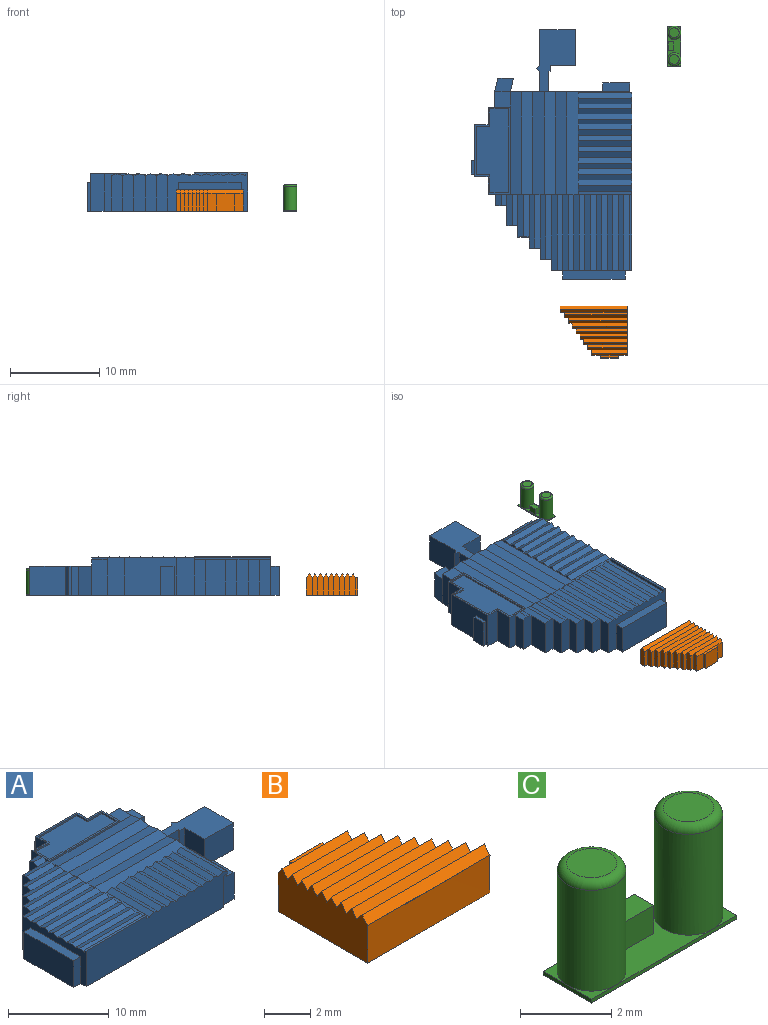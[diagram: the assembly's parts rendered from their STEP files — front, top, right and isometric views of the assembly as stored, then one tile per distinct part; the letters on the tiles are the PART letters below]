
ASSEMBLY  parts=3 mates=2
PART A: 138 faces, bbox 28x18x4.3 mm
  f0: plane 3.25x0.4mm, normal (1,0,0), area 1.3mm2, adj f44,f46,f65,f137
  f1: plane 4x3.25mm, normal (0,-1,0), area 13mm2, adj f2,f6,f65,f136
  f2: plane 4x3.25mm, normal (1,0,0), area 13mm2, adj f1,f7,f65,f136
  f3: plane 3.25x2.29mm, normal (0,-1,0), area 7.5mm2, adj f4,f39,f65,f136
  f4: plane 3.25x0.2mm, normal (-1,0,0), area 0.7mm2, adj f3,f5,f65,f136
  f5: plane 3.25x0.67mm, normal (0,-1,0), area 2.2mm2, adj f4,f6,f65,f136
  f6: plane 3.25x2.8mm, normal (-1,0,0), area 9.1mm2, adj f1,f5,f65,f136
  f7: plane 4x3.25mm, normal (0,1,0), area 13mm2, adj f2,f8,f65,f136
  f8: plane 3.25x0.38mm, normal (0.75,0.66,0), area 1.6mm2, adj f7,f9,f65,f136
  f9: plane 3.25x0.38mm, normal (-0.75,0.66,0), area 1.6mm2, adj f8,f10,f65,f136
  f10: plane 3.25x2.29mm, normal (0,1,0), area 7.5mm2, adj f9,f39,f65,f136
  f11: plane 3.25x1.5mm, normal (-0.22,-0.97,0), area 5mm2, adj f12,f39,f65,f135
  f12: plane 3.25x1.75mm, normal (1,0,0), area 5.7mm2, adj f11,f13,f65,f135
  f13: plane 3.25x1.5mm, normal (0.22,0.97,0), area 5mm2, adj f12,f40,f65,f135
  f14: plane 7.25x0.63mm, normal (0,-0.3,0.95), area 4.8mm2, adj f15,f29,f59,f109,f134
  f15: plane 7.25x0.63mm, normal (0,0.3,0.95), area 4.8mm2, adj f14,f16,f28,f58,f59,f109
  f16: plane 6x0.63mm, normal (0,-0.3,0.95), area 3.9mm2, adj f15,f17,f28,f57,f111
  f17: plane 6x0.63mm, normal (0,0.3,0.95), area 3.9mm2, adj f16,f18,f31,f56,f57,f111
  f18: plane 4.75x0.63mm, normal (0,-0.3,0.95), area 3.1mm2, adj f17,f19,f31,f55,f112
  f19: plane 4.75x0.63mm, normal (0,0.3,0.95), area 3.1mm2, adj f18,f20,f30,f54,f55,f112
  f20: plane 3.5x0.63mm, normal (0,-0.3,0.95), area 2.3mm2, adj f19,f21,f30,f53,f113
  f21: plane 3.5x0.63mm, normal (0,0.3,0.95), area 2.3mm2, adj f20,f22,f49,f52,f53,f113
  f22: plane 1.25x0.63mm, normal (0,-0.3,0.95), area 0.8mm2, adj f21,f23,f49,f51
  f23: plane 1.25x0.63mm, normal (0,0.3,0.95), area 0.8mm2, adj f22,f25,f50,f51
  f24: plane 6x0.39mm, normal (0,0,1), area 2.3mm2, adj f64,f68,f100,f107,f114,f115,f116,f117
  f25: plane 4.2x1.48mm, normal (-1,0,0), area 3.6mm2, adj f23,f48,f50,f65,f98
  f26: plane 0.84x0.2mm, normal (-1,0,0), area 0.1mm2, adj f100,f105,f132,f133
  f27: plane 0.65x0.16mm, normal (-1,0,0), area 0mm2, adj f100,f130,f131
  f28: plane 0.84x0.2mm, normal (-1,0,0), area 0.1mm2, adj f15,f16,f103,f104
  f29: plane 0.61x0.15mm, normal (-1,0,0), area 0mm2, adj f14,f104,f134
  f30: plane 0.84x0.2mm, normal (-1,0,0), area 0.1mm2, adj f19,f20,f101,f102
  f31: plane 0.56x0.13mm, normal (-1,0,0), area 0mm2, adj f17,f18,f102
  f32: plane 5.75x0.1mm, normal (0,0,1), area 0.6mm2, adj f37,f39,f67,f100
  f33: plane 3.25x3mm, normal (1,0,0), area 9.8mm2, adj f34,f37,f65,f106
  f34: plane 3.25x1mm, normal (0,1,0), area 3.2mm2, adj f33,f39,f65,f106
  f35: plane 1.75x1.7mm, normal (0,0,1), area 3mm2, adj f39,f40,f41,f101
  f36: plane 7x3.25mm, normal (-1,0,0), area 22.8mm2, adj f61,f62,f65,f88
  f37: plane 4x1.75mm, normal (0,-1,0), area 6.1mm2, adj f32,f33,f38,f39,f65,f66,f67,f106
  f38: plane 3.79x0.25mm, normal (1,0,0), area 0.9mm2, adj f37,f64,f65,f66
  f39: plane 15.1x4.2mm, normal (1,0,0), area 42.5mm2, adj f3,f10,f11,f32,f34,f35,f37,f40
  f40: plane 4x1.7mm, normal (0,1,0), area 6.8mm2, adj f13,f35,f39,f41,f65
  f41: plane 4.2x2.5mm, normal (1,0,0), area 3.5mm2, adj f35,f40,f42,f65,f96,f98
  f42: plane 4.2x2mm, normal (0,1,0), area 8.4mm2, adj f41,f43,f65,f98
  f43: plane 4.2x1.5mm, normal (1,0,0), area 6.3mm2, adj f42,f46,f65,f98
  f44: plane 3.25x1.5mm, normal (0,1,0), area 4.9mm2, adj f0,f45,f65,f137
  f45: plane 3.25x0.4mm, normal (-1,0,0), area 1.3mm2, adj f44,f46,f65,f137
  f46: plane 5.8x4.2mm, normal (0,1,0), area 19.5mm2, adj f0,f43,f45,f47,f65,f98,f137
  f47: plane 4.2x1.5mm, normal (-1,0,0), area 6.3mm2, adj f46,f48,f65,f98
  f48: plane 4.2x2mm, normal (0,1,0), area 8.4mm2, adj f25,f47,f65,f98
  f49: plane 1.03x0.2mm, normal (-1,0,0), area 0.1mm2, adj f21,f22,f96,f98
  f50: plane 4x1.25mm, normal (0,1,0), area 5mm2, adj f23,f25,f51,f65
  f51: plane 4.2x1.25mm, normal (-1,0,0), area 5.1mm2, adj f22,f23,f50,f52,f65
  f52: plane 4x2.25mm, normal (0,1,0), area 9mm2, adj f21,f51,f53,f65
  f53: plane 4.2x1.25mm, normal (-1,0,0), area 5.1mm2, adj f20,f21,f52,f54,f65
  f54: plane 4x1.25mm, normal (0,1,0), area 5mm2, adj f19,f53,f55,f65
  f55: plane 4.2x1.25mm, normal (-1,0,0), area 5.1mm2, adj f18,f19,f54,f56,f65
  f56: plane 4x1.25mm, normal (0,1,0), area 5mm2, adj f17,f55,f57,f65
  f57: plane 4.2x1.25mm, normal (-1,0,0), area 5.1mm2, adj f16,f17,f56,f58,f65
  f58: plane 4x1.25mm, normal (0,1,0), area 5mm2, adj f15,f57,f59,f65
  f59: plane 4.2x1.25mm, normal (-1,0,0), area 5.1mm2, adj f14,f15,f58,f60,f65
  f60: plane 4x1.25mm, normal (0,1,0), area 5mm2, adj f59,f63,f65,f134
  f61: plane 3.25x1mm, normal (0,1,0), area 3.3mm2, adj f36,f63,f65,f88
  f62: plane 3.25x1mm, normal (0,-1,0), area 3.3mm2, adj f36,f63,f65,f88
  f63: plane 9x4.32mm, normal (-1,0,0), area 14.2mm2, adj f60,f61,f62,f64,f65,f88,f119,f120
  f64: plane 19.9x4.32mm, normal (0,-1,0), area 81.6mm2, adj f24,f38,f63,f65,f66,f67,f68,f69
  f65: plane 27.96x18mm, normal (0,0,-1), area 329.8mm2, adj f0,f1,f2,f3,f4,f5,f6,f7
  f66: plane 0.65x0.25mm, normal (0,0,-1), area 0.2mm2, adj f37,f38,f64,f67
  f67: plane 6x0.22mm, normal (1,0,0), area 0.1mm2, adj f32,f37,f64,f66,f69,f87
  f68: plane 6x0.02mm, normal (-1,0,0), area 0.1mm2, adj f24,f64,f86,f87
  f69: plane 6x0.63mm, normal (0.44,0,0.9), area 4.2mm2, adj f64,f67,f70,f87
  f70: plane 6x0.63mm, normal (-0.43,0,0.9), area 4.2mm2, adj f64,f69,f71,f87
  f71: plane 6x0.56mm, normal (0.47,0,0.88), area 3.8mm2, adj f64,f70,f72,f87
  f72: plane 6x0.56mm, normal (-0.47,0,0.88), area 3.8mm2, adj f64,f71,f73,f87
  f73: plane 6x0.56mm, normal (0.47,0,0.88), area 3.8mm2, adj f64,f72,f74,f87
  f74: plane 6x0.56mm, normal (-0.47,0,0.88), area 3.8mm2, adj f64,f73,f75,f87
  f75: plane 6x0.63mm, normal (0.43,0,0.9), area 4.2mm2, adj f64,f74,f76,f87
  f76: plane 6x0.63mm, normal (-0.43,0,0.9), area 4.2mm2, adj f64,f75,f77,f87
  f77: plane 6x0.63mm, normal (0.43,0,0.9), area 4.2mm2, adj f64,f76,f78,f87
  f78: plane 6x0.63mm, normal (-0.43,0,0.9), area 4.2mm2, adj f64,f77,f79,f87
  f79: plane 6x0.63mm, normal (0.43,0,0.9), area 4.2mm2, adj f64,f78,f80,f87
  f80: plane 6x0.63mm, normal (-0.43,0,0.9), area 4.2mm2, adj f64,f79,f81,f87
  f81: plane 6x0.63mm, normal (0.43,0,0.9), area 4.2mm2, adj f64,f80,f82,f87
  f82: plane 6x0.63mm, normal (-0.43,0,0.9), area 4.2mm2, adj f64,f81,f83,f87
  f83: plane 6x0.63mm, normal (0.43,0,0.9), area 4.2mm2, adj f64,f82,f84,f87
  f84: plane 6x0.63mm, normal (-0.43,0,0.9), area 4.2mm2, adj f64,f83,f85,f87
  f85: plane 6x0.63mm, normal (0.43,0,0.9), area 4.2mm2, adj f64,f84,f86,f87
  f86: plane 6x0.63mm, normal (-0.43,0,0.9), area 4.2mm2, adj f64,f68,f85,f87
  f87: plane 11.01x0.32mm, normal (0,1,0), area 1.8mm2, adj f67,f68,f69,f70,f71,f72,f73,f74
  f88: plane 7x1mm, normal (0,0,1), area 7mm2, adj f36,f61,f62,f63
  f89: plane 9.4x0.2mm, normal (0,1,0), area 1.9mm2, adj f90,f97,f98,f99
  f90: plane 2.1x0.2mm, normal (1,0,0), area 0.4mm2, adj f89,f91,f98,f99
  f91: plane 2x0.2mm, normal (0,-1,0), area 0.4mm2, adj f90,f92,f98,f99
  f92: plane 1.5x0.2mm, normal (1,0,0), area 0.3mm2, adj f91,f93,f98,f99
  f93: plane 5.4x0.2mm, normal (0,-1,0), area 1.1mm2, adj f92,f94,f98,f99
  f94: plane 1.5x0.2mm, normal (-1,0,0), area 0.3mm2, adj f93,f95,f98,f99
  f95: plane 2x0.2mm, normal (0,-1,0), area 0.4mm2, adj f94,f97,f98,f99
  f96: plane 9.8x0.2mm, normal (0,-1,0), area 2mm2, adj f41,f49,f98,f101,f113
  f97: plane 2.1x0.2mm, normal (-1,0,0), area 0.4mm2, adj f89,f95,f98,f99
  f98: plane 9.8x4mm, normal (0,0,1), area 5.4mm2, adj f25,f41,f42,f43,f46,f47,f48,f49
  f99: plane 9.4x3.6mm, normal (0,0,1), area 27.8mm2, adj f89,f90,f91,f92,f93,f94,f95,f97
  f100: plane 11.5x1.27mm, normal (0,-0.16,0.99), area 14.8mm2, adj f24,f26,f27,f32,f39,f87,f105,f107
  f101: plane 11.5x1.27mm, normal (0,0.16,0.99), area 14.7mm2, adj f30,f35,f39,f96,f102,f113
  f102: plane 11.5x1.27mm, normal (0,-0.16,0.99), area 14.8mm2, adj f30,f31,f39,f101,f103,f111,f112
  f103: plane 11.5x1.26mm, normal (0,0.16,0.99), area 14.7mm2, adj f28,f39,f102,f104,f111
  f104: plane 11.5x1.27mm, normal (0,-0.16,0.99), area 14.8mm2, adj f28,f29,f39,f103,f105,f109,f110
  f105: plane 11.5x1.26mm, normal (0,0.16,0.99), area 14.7mm2, adj f26,f39,f100,f104,f110
  f106: plane 3x1mm, normal (0,0,1), area 3mm2, adj f33,f34,f37,f39
  f107: plane 1.09x0.2mm, normal (1,0,0), area 0.1mm2, adj f24,f100,f129,f130
  f108: plane 0.19x0.04mm, normal (1,0,0), area 0mm2, adj f100,f131,f132
  f109: plane 0.23x0.06mm, normal (1,0,0), area 0mm2, adj f14,f15,f104
  f110: plane 0.84x0.2mm, normal (1,0,0), area 0.1mm2, adj f104,f105,f133,f134
  f111: plane 0.84x0.2mm, normal (1,0,0), area 0.1mm2, adj f16,f17,f102,f103
  f112: plane 0.27x0.07mm, normal (1,0,0), area 0mm2, adj f18,f19,f102
  f113: plane 0.57x0.2mm, normal (1,0,0), area 0.1mm2, adj f20,f21,f96,f101
  f114: plane 1.25x0.2mm, normal (1,0,0), area 0.1mm2, adj f24,f127,f128
  f115: plane 1.25x0.2mm, normal (1,0,0), area 0.1mm2, adj f24,f125,f126
  f116: plane 1.25x0.2mm, normal (1,0,0), area 0.1mm2, adj f24,f123,f124
  f117: plane 1.25x0.2mm, normal (1,0,0), area 0.1mm2, adj f24,f121,f122
  f118: plane 0.32x0.25mm, normal (1,0,0), area 0.1mm2, adj f24,f64,f119,f120
  f119: plane 8.5x0.25mm, normal (0,0,1), area 2.1mm2, adj f63,f64,f118,f120
  f120: plane 8.5x0.32mm, normal (0,1,0.01), area 2.7mm2, adj f63,f118,f119,f121
  f121: plane 8.5x0.63mm, normal (0,-0.3,0.95), area 5.6mm2, adj f63,f117,f120,f122
  f122: plane 8.5x0.63mm, normal (0,0.3,0.95), area 5.6mm2, adj f63,f117,f121,f123
  f123: plane 8.5x0.63mm, normal (0,-0.3,0.95), area 5.6mm2, adj f63,f116,f122,f124
  f124: plane 8.5x0.63mm, normal (0,0.3,0.95), area 5.6mm2, adj f63,f116,f123,f125
  f125: plane 8.5x0.63mm, normal (0,-0.3,0.95), area 5.6mm2, adj f63,f115,f124,f126
  f126: plane 8.5x0.63mm, normal (0,0.3,0.95), area 5.6mm2, adj f63,f115,f125,f127
  f127: plane 8.5x0.63mm, normal (0,-0.3,0.95), area 5.6mm2, adj f63,f114,f126,f128
  f128: plane 8.5x0.63mm, normal (0,0.3,0.95), area 5.6mm2, adj f63,f114,f127,f129
  f129: plane 8.5x0.63mm, normal (0,-0.3,0.95), area 5.6mm2, adj f63,f107,f128,f130
  f130: plane 8.5x0.63mm, normal (0,0.3,0.95), area 5.6mm2, adj f27,f63,f107,f129,f131
  f131: plane 8.5x0.63mm, normal (0,-0.3,0.95), area 5.6mm2, adj f27,f63,f108,f130,f132
  f132: plane 8.5x0.63mm, normal (0,0.3,0.95), area 5.6mm2, adj f26,f63,f108,f131,f133
  f133: plane 8.5x0.63mm, normal (0,-0.3,0.95), area 5.6mm2, adj f26,f63,f110,f132,f134
  f134: plane 8.5x0.63mm, normal (0,0.3,0.95), area 5.6mm2, adj f14,f29,f60,f63,f110,f133
  f135: plane 2.1x1.5mm, normal (0,0,1), area 2.6mm2, adj f11,f12,f13,f39
  f136: plane 6.96x4.38mm, normal (0,0,1), area 19.2mm2, adj f1,f2,f3,f4,f5,f6,f7,f8
  f137: plane 1.5x0.4mm, normal (0,0,1), area 0.6mm2, adj f0,f44,f45,f46
PART B: 45 faces, bbox 7.5x5.8x2.4 mm
  f0: plane 2.42x0.71mm, normal (1,0,0), area 1.6mm2, adj f16,f24,f25,f41,f43,f44
  f1: plane 4x0.41mm, normal (0,-0.75,0.66), area 2.1mm2, adj f2,f4,f17,f23
  f2: plane 4.02x0.43mm, normal (0,0.85,0.52), area 1.9mm2, adj f1,f17,f18,f22,f23,f40
  f3: plane 4.43x0.41mm, normal (0,-0.77,0.64), area 2.3mm2, adj f4,f5,f23,f38
  f4: plane 4.43x0.41mm, normal (0,0.83,0.55), area 2.1mm2, adj f1,f3,f23,f38,f39
  f5: plane 4.86x0.41mm, normal (0,0.83,0.55), area 2.3mm2, adj f3,f6,f23,f36,f37,f38
  f6: plane 4.86x0.41mm, normal (0,-0.77,0.64), area 2.5mm2, adj f5,f7,f23,f36
  f7: plane 5.29x0.41mm, normal (0,0.83,0.55), area 2.5mm2, adj f6,f8,f23,f34,f35,f36
  f8: plane 5.29x0.41mm, normal (0,-0.77,0.64), area 2.8mm2, adj f7,f9,f23,f34
  f9: plane 5.72x0.41mm, normal (0,0.83,0.55), area 2.7mm2, adj f8,f10,f23,f32,f33,f34
  f10: plane 5.72x0.41mm, normal (0,-0.77,0.64), area 3mm2, adj f9,f11,f23,f32
  f11: plane 6.15x0.41mm, normal (0,0.83,0.55), area 3mm2, adj f10,f12,f23,f30,f31,f32
  f12: plane 6.15x0.41mm, normal (0,-0.77,0.64), area 3.2mm2, adj f11,f13,f23,f30
  f13: plane 6.58x0.41mm, normal (0,0.84,0.55), area 3.1mm2, adj f12,f14,f23,f28,f29,f30
  f14: plane 6.58x0.41mm, normal (0,-0.76,0.65), area 3.5mm2, adj f13,f15,f23,f28
  f15: plane 7.01x0.42mm, normal (0,0.78,0.62), area 3.6mm2, adj f14,f16,f23,f26,f27,f28
  f16: plane 7.5x0.42mm, normal (0,-0.82,0.57), area 3.4mm2, adj f0,f15,f23,f25,f26,f43
  f17: plane 2.41x0.6mm, normal (1,0,0), area 1.3mm2, adj f1,f2,f18,f39,f41
  f18: plane 2.02x1.02mm, normal (0,1,0), area 2mm2, adj f2,f17,f19,f41
  f19: plane 2x0.3mm, normal (1,0,0), area 0.6mm2, adj f18,f20,f40,f41
  f20: plane 2x2mm, normal (0,1,0), area 4mm2, adj f19,f21,f40,f41
  f21: plane 2x0.3mm, normal (-1,0,0), area 0.6mm2, adj f20,f22,f40,f41
  f22: plane 2x1mm, normal (0,1,0), area 2mm2, adj f2,f21,f23,f41
  f23: plane 5.5x2.4mm, normal (-1,0,0), area 12.1mm2, adj f1,f2,f3,f4,f5,f6,f7,f8
  f24: plane 7.5x2mm, normal (0,-1,0), area 15mm2, adj f0,f23,f41,f42
  f25: plane 2.02x0.49mm, normal (0,1,0), area 1mm2, adj f0,f16,f26,f41
  f26: plane 2.42x0.6mm, normal (1,0,0), area 1.3mm2, adj f15,f16,f25,f27,f41
  f27: plane 2.01x0.43mm, normal (0,1,0), area 0.9mm2, adj f15,f26,f28,f41
  f28: plane 2.41x0.6mm, normal (1,0,0), area 1.3mm2, adj f13,f14,f15,f27,f29,f41
  f29: plane 2.02x0.43mm, normal (0,1,0), area 0.9mm2, adj f13,f28,f30,f41
  f30: plane 2.41x0.6mm, normal (1,0,0), area 1.3mm2, adj f11,f12,f13,f29,f31,f41
  f31: plane 2.01x0.43mm, normal (0,1,0), area 0.9mm2, adj f11,f30,f32,f41
  f32: plane 2.41x0.6mm, normal (1,0,0), area 1.3mm2, adj f9,f10,f11,f31,f33,f41
  f33: plane 2.01x0.43mm, normal (0,1,0), area 0.9mm2, adj f9,f32,f34,f41
  f34: plane 2.41x0.6mm, normal (1,0,0), area 1.3mm2, adj f7,f8,f9,f33,f35,f41
  f35: plane 2.01x0.43mm, normal (0,1,0), area 0.9mm2, adj f7,f34,f36,f41
  f36: plane 2.41x0.6mm, normal (1,0,0), area 1.3mm2, adj f5,f6,f7,f35,f37,f41
  f37: plane 2.01x0.43mm, normal (0,1,0), area 0.9mm2, adj f5,f36,f38,f41
  f38: plane 2.41x0.6mm, normal (1,0,0), area 1.3mm2, adj f3,f4,f5,f37,f39,f41
  f39: plane 2.01x0.43mm, normal (0,1,0), area 0.9mm2, adj f4,f17,f38,f41
  f40: plane 2.01x0.31mm, normal (0,0,1), area 0.6mm2, adj f2,f19,f20,f21
  f41: plane 7.5x5.8mm, normal (0,0,-1), area 32.3mm2, adj f0,f17,f18,f19,f20,f21,f22,f23
  f42: plane 7.5x0.02mm, normal (0,0,-1), area 0.1mm2, adj f24,f44
  f43: plane 7.5x0.42mm, normal (0,0.74,0.67), area 4mm2, adj f0,f16,f23,f44
  f44: plane 7.5x0.42mm, normal (0,-0.76,0.65), area 4.1mm2, adj f0,f23,f42,f43
PART C: 21 faces, bbox 4.6x1.6x3 mm
  f0: cylinder r=0.75mm len=2.7mm, axis (0,0,-1), area 12.7mm2, adj f2,f5,f6,f13
  f1: plane 1.1x1.1mm, normal (0,0,1), area 1mm2, adj f2
  f2: torus R=0.55mm, axis (0,0,1), area 1.3mm2, adj f0,f1
  f3: plane 4.5x0.1mm, normal (0,1,0), area 0.5mm2, adj f5,f7,f11,f12,f13,f15
  f4: plane 4.5x0.1mm, normal (0,-1,0), area 0.5mm2, adj f6,f7,f11,f13,f14,f15
  f5: plane 0.75x0.75mm, normal (0,0,1), area 0.1mm2, adj f0,f3,f7
  f6: plane 0.75x0.75mm, normal (0,0,1), area 0.1mm2, adj f0,f4,f7
  f7: plane 1.5x0.1mm, normal (-1,0,0), area 0.2mm2, adj f3,f4,f5,f6,f15
  f8: cylinder r=0.75mm len=2.7mm, axis (0,0,-1), area 12.7mm2, adj f10,f12,f13,f14
  f9: plane 1.1x1.1mm, normal (0,0,1), area 1mm2, adj f10
  f10: torus R=0.55mm, axis (0,0,1), area 1.3mm2, adj f8,f9
  f11: plane 1.5x0.1mm, normal (1,0,0), area 0.2mm2, adj f3,f4,f12,f14,f15
  f12: plane 0.75x0.75mm, normal (0,0,1), area 0.1mm2, adj f3,f8,f11
  f13: plane 3x1.5mm, normal (0,0,1), area 2.2mm2, adj f0,f3,f4,f8,f16,f17,f18,f19
  f14: plane 0.75x0.75mm, normal (0,0,1), area 0.1mm2, adj f4,f8,f11
  f15: plane 4.5x1.5mm, normal (0,0,-1), area 6.7mm2, adj f3,f4,f7,f11
  f16: plane 0.75x0.6mm, normal (1,0,0), area 0.4mm2, adj f13,f17,f19,f20
  f17: plane 0.96x0.75mm, normal (0,1,0), area 0.7mm2, adj f13,f16,f18,f20
  f18: plane 0.75x0.6mm, normal (-1,0,0), area 0.4mm2, adj f13,f17,f19,f20
  f19: plane 0.96x0.75mm, normal (0,-1,0), area 0.7mm2, adj f13,f16,f18,f20
  f20: plane 0.96x0.6mm, normal (0,0,1), area 0.6mm2, adj f16,f17,f18,f19
PLACE A rot(axis=(0,0,1),90deg) t=(-5.53,16,0)mm
PLACE B rot(axis=(0,0,1),180deg) t=(-0.78,-0.25,0)mm
PLACE C rot(axis=(0,0,1),90deg) t=(8.22,31.62,0)mm
MATE planar B.f41 <-> A.f65  axis (0,0,-1) through (-0.78,2.5,0)mm
MATE fastened C.f15 <-> A.f65  axis (0,0,-1) through (8.22,31.62,0)mm
